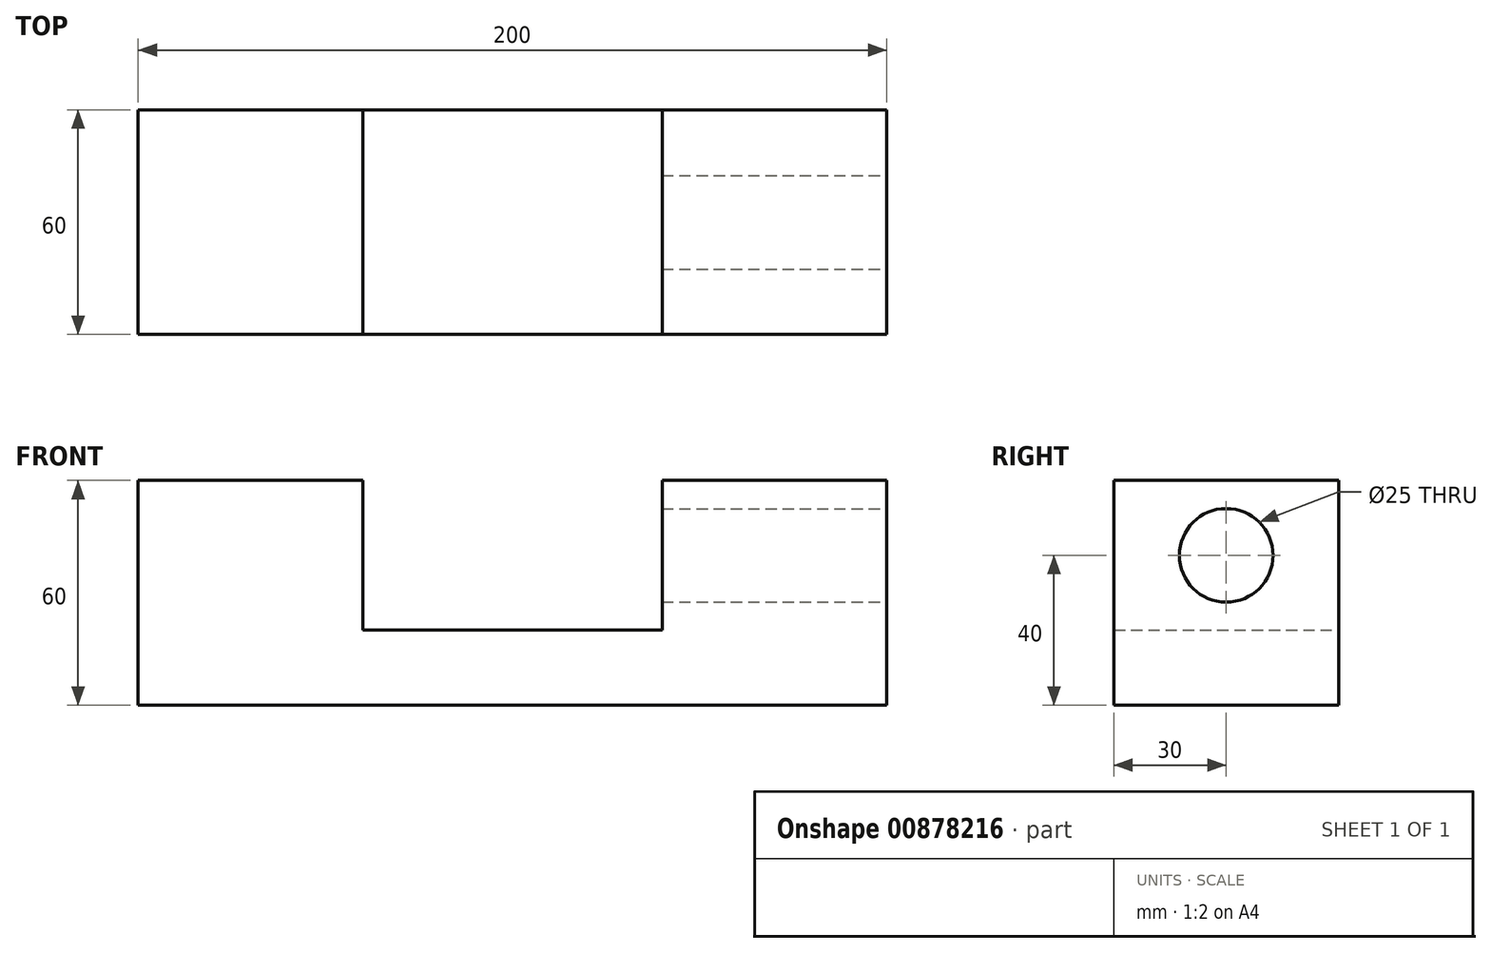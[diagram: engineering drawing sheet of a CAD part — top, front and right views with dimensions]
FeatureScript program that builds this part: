
annotation { "Feature Type Name" : "Feature", "Feature Type Description" : "" }
export const myFeature = defineFeature(function(context is Context, id is Id, definition is map)
    precondition{}
    {
        {
            var Q0;
            Q0=qCreatedBy(makeId("Front.planeOp"),FACE);
            var sketch = newSketch(context, id + "F0", { "sketchPlane" : qUnion([Q0])});
            skLineSegment(sketch, "E0.bottom", {"start": v(0, 0) * mm, "end": v(200, 0) * mm});
            skLineSegment(sketch, "E0.left", {"start": v(0, 0) * mm, "end": v(0, 60) * mm});
            skLineSegment(sketch, "E0.right", {"start": v(200, 0) * mm, "end": v(200, 60) * mm});
            skLineSegment(sketch, "E1", {"start": v(0, 60) * mm, "end": v(60, 60) * mm});
            skLineSegment(sketch, "E2", {"start": v(60, 60) * mm, "end": v(60, 20) * mm});
            skLineSegment(sketch, "E3", {"start": v(60, 20) * mm, "end": v(140, 20) * mm});
            skLineSegment(sketch, "E4", {"start": v(140, 20) * mm, "end": v(140, 60) * mm});
            skLineSegment(sketch, "E5", {"start": v(140, 60) * mm, "end": v(200, 60) * mm});
            skSolve(sketch);
        }
        {
            var Q0;
            Q0=makeQuery(id+"F0.imprint","IMPRINT",FACE,{"disambiguationData":[TD([[makeQuery(id+"F0.imprint","IMPRINT",EDGE,{"derivedFrom":sQuery(id+"F0.wireOp",EDGE,"E0.bottom")}),1.0]])]});
            extrude(context, id + "F1", {"entities" : qUnion([Q0]), "depth" : 60 * mm, "offsetDistance" : 25 * mm});
        }
        {
            var Q0;
            Q0=makeQuery(id+"F1.opExtrude","SWEPT_FACE",FACE,{"disambiguationData":[OSD([sQuery(id+"F0.wireOp",EDGE,"E0.right")])]});
            var sketch = newSketch(context, id + "F2", { "sketchPlane" : qUnion([Q0])});
            skCircle(sketch, "E6", {"center": v(-30, 40) * mm, "radius": 12.5 * mm});
            skPoint(sketch, "E7.orphan", {"position": v(-30, 60) * mm});
            skSolve(sketch);
        }
        {
            var Q0;
            Q0=makeQuery(id+"F2.imprint","IMPRINT",FACE,{"disambiguationData":[TD([[makeQuery(id+"F2.imprint","IMPRINT",EDGE,{"derivedFrom":sQuery(id+"F2.wireOp",EDGE,"E6")}),1.0]])]});
            extrude(context, id + "F3", {"entities" : qUnion([Q0]), "operationType" : NewBodyOperationType.REMOVE, "oppositeDirection" : true, "depth" : 82.6 * mm, "offsetDistance" : 25 * mm});
        }
    });
